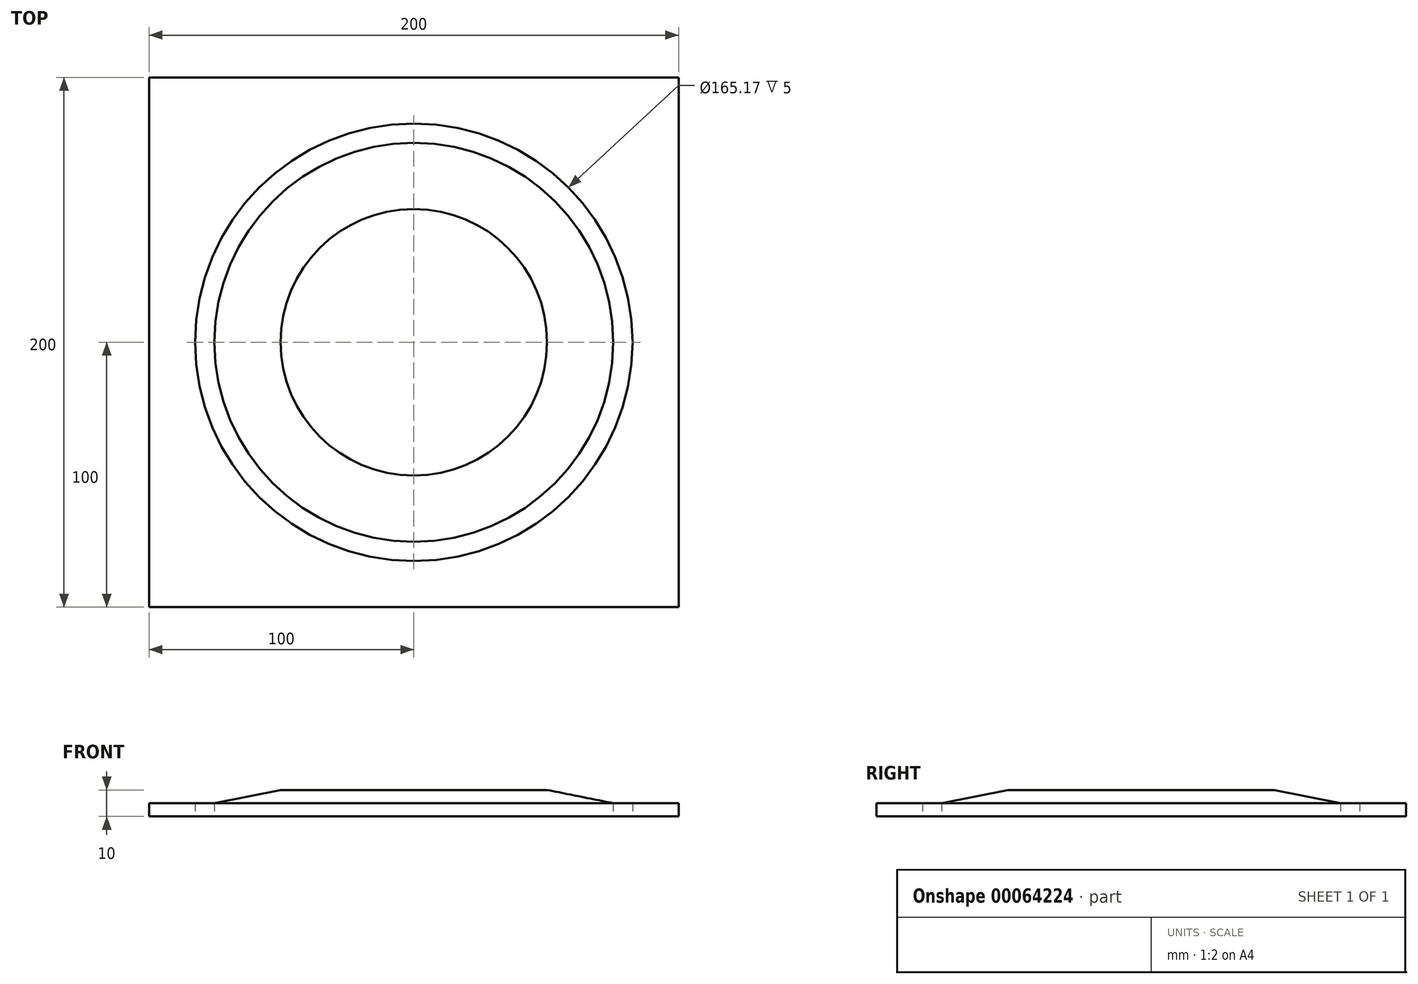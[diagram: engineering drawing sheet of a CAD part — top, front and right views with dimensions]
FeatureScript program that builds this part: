
annotation { "Feature Type Name" : "Feature", "Feature Type Description" : "" }
export const myFeature = defineFeature(function(context is Context, id is Id, definition is map)
    precondition{}
    {
        {
            var Q0;
            Q0=qCreatedBy(makeId("Top.planeOp"),FACE);
            var sketch = newSketch(context, id + "F0", { "sketchPlane" : qUnion([Q0])});
            skCircle(sketch, "E0", {"center": v(0, 0) * mm, "radius": 75.3 * mm});
            skSolve(sketch);
        }
        {
            var Q0;
            Q0=makeQuery(id+"F0.imprint","IMPRINT",FACE,{"disambiguationData":[TD([[makeQuery(id+"F0.imprint","IMPRINT",EDGE,{"derivedFrom":sQuery(id+"F0.wireOp",EDGE,"E0")}),1.0]])]});
            extrude(context, id + "F1", {"entities" : qUnion([Q0]), "depth" : 10 * mm});
        }
        {
            var Q0;
            Q0=makeQuery(id+"F1.opExtrude","CAP_EDGE",EDGE,{"disambiguationData":[OSD([sQuery(id+"F0.wireOp",EDGE,"E0")])],"isStart":false});
            chamfer(context, id + "F2", {"entities" : qUnion([Q0]), "chamferType" : ChamferType.TWO_OFFSETS, "width1" : 25 * mm, "oppositeDirection" : false, "width2" : 5 * mm});
        }
        {
            var Q0;
            Q0=makeQuery(id+"F1.opExtrude","CAP_FACE",FACE,{"disambiguationData":[OSD([sQuery(id+"F0.wireOp",EDGE,"E0")])],"isStart":true});
            var sketch = newSketch(context, id + "F3", { "sketchPlane" : qUnion([Q0])});
            skCircle(sketch, "E1", {"center": v(0, 0) * mm, "radius": 82.59 * mm});
            skLineSegment(sketch, "E2.rect.bottom", {"start": v(100, -100) * mm, "end": v(-100, -100) * mm});
            skLineSegment(sketch, "E2.rect.top", {"start": v(100, 100) * mm, "end": v(-100, 100) * mm});
            skLineSegment(sketch, "E2.rect.left", {"start": v(100, -100) * mm, "end": v(100, 100) * mm});
            skLineSegment(sketch, "E2.rect.right", {"start": v(-100, -100) * mm, "end": v(-100, 100) * mm});
            skSolve(sketch);
        }
        {
            var Q0;
            Q0=makeQuery(id+"F3.imprint","IMPRINT",FACE,{"disambiguationData":[TD([[makeQuery(id+"F3.imprint","IMPRINT",EDGE,{"derivedFrom":sQuery(id+"F3.wireOp",EDGE,"E1")}),-1.0]])]});
            extrude(context, id + "F4", {"entities" : qUnion([Q0]), "oppositeDirection" : true, "depth" : 5 * mm});
        }
    });
